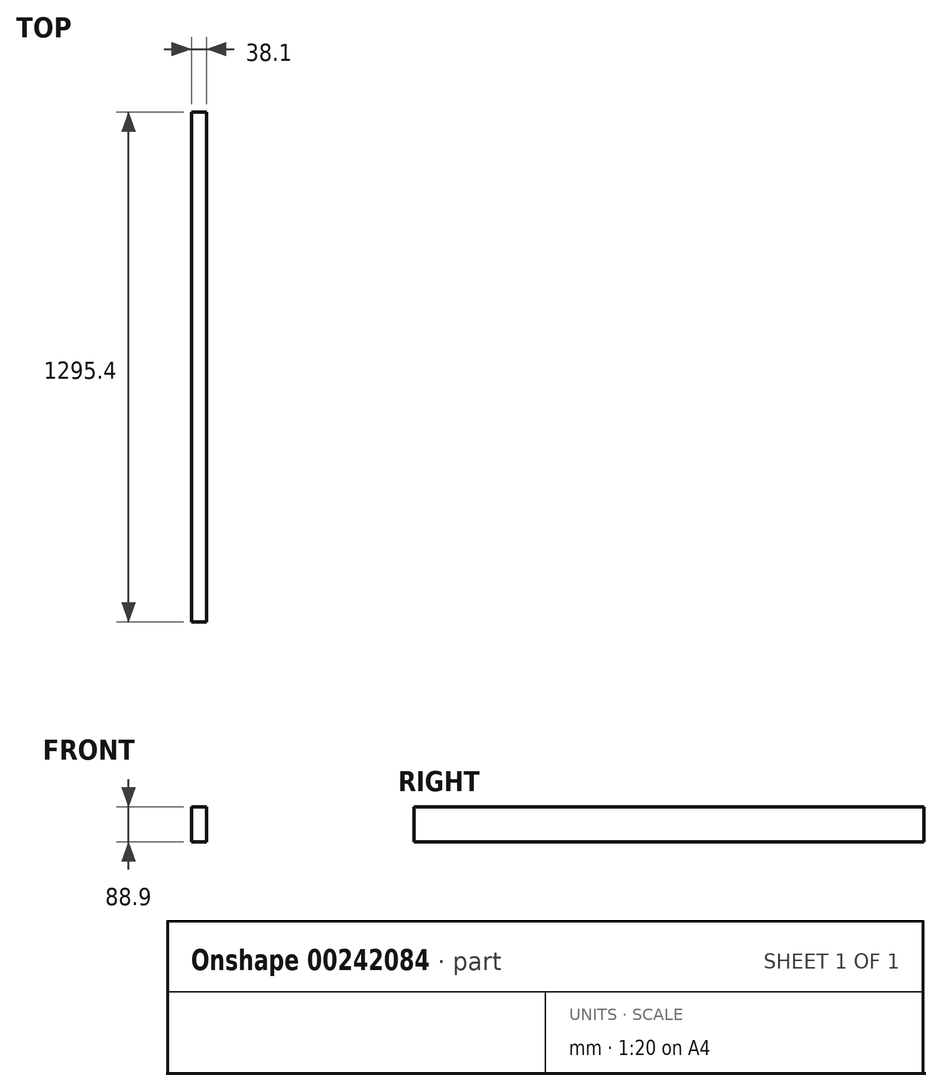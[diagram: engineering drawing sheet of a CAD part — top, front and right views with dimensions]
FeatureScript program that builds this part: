
annotation { "Feature Type Name" : "Feature", "Feature Type Description" : "" }
export const myFeature = defineFeature(function(context is Context, id is Id, definition is map)
    precondition{}
    {
        {
            var Q0;
            Q0=qCreatedBy(makeId("Front.planeOp"),FACE);
            var sketch = newSketch(context, id + "F0", { "sketchPlane" : qUnion([Q0])});
            skLineSegment(sketch, "E0.bottom", {"start": v(-8.3, 73.65) * mm, "end": v(29.8, 73.65) * mm});
            skLineSegment(sketch, "E0.top", {"start": v(-8.3, -15.25) * mm, "end": v(29.8, -15.25) * mm});
            skLineSegment(sketch, "E0.left", {"start": v(-8.3, 73.65) * mm, "end": v(-8.3, -15.25) * mm});
            skLineSegment(sketch, "E0.right", {"start": v(29.8, 73.65) * mm, "end": v(29.8, -15.25) * mm});
            skSolve(sketch);
        }
        {
            var Q0;
            Q0=makeQuery(id+"F0.imprint","IMPRINT",FACE,{"disambiguationData":[TD([[makeQuery(id+"F0.imprint","IMPRINT",EDGE,{"derivedFrom":sQuery(id+"F0.wireOp",EDGE,"E0.bottom")}),-1.0]])]});
            extrude(context, id + "F1", {"entities" : qUnion([Q0]), "depth" : 1295.4 * mm});
        }
    });
